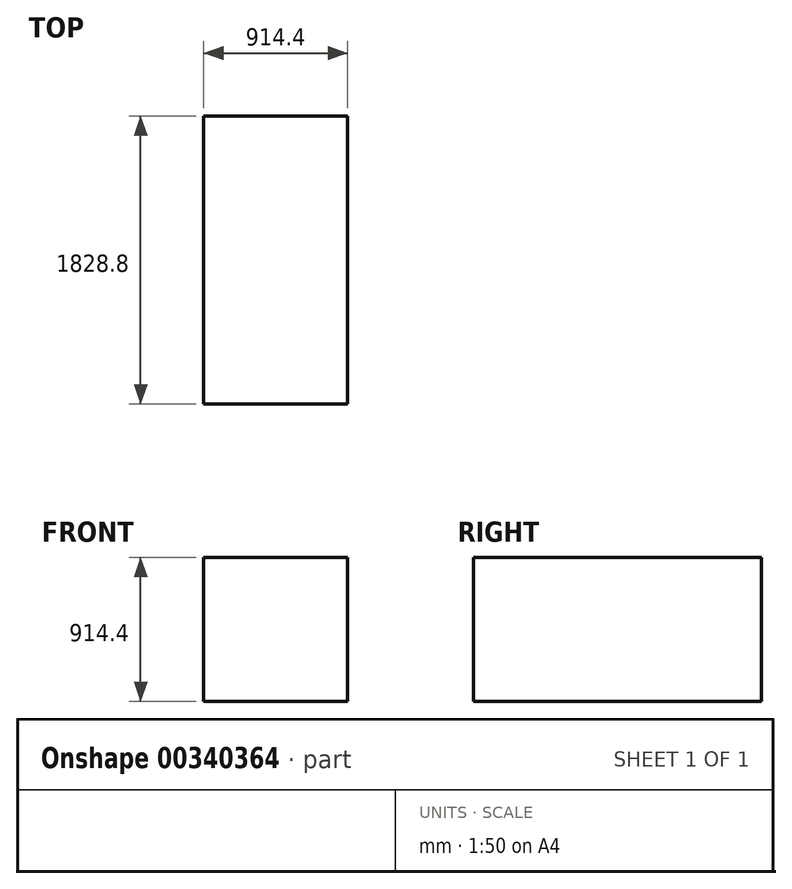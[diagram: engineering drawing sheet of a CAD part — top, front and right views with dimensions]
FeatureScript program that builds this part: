
annotation { "Feature Type Name" : "Feature", "Feature Type Description" : "" }
export const myFeature = defineFeature(function(context is Context, id is Id, definition is map)
    precondition{}
    {
        {
            var Q0;
            Q0=qCreatedBy(makeId("Top.planeOp"),FACE);
            var sketch = newSketch(context, id + "F0", { "sketchPlane" : qUnion([Q0])});
            skLineSegment(sketch, "E0.bottom", {"start": v(457.2, 914.4) * mm, "end": v(-457.2, 914.4) * mm});
            skLineSegment(sketch, "E0.top", {"start": v(457.2, -914.4) * mm, "end": v(-457.2, -914.4) * mm});
            skLineSegment(sketch, "E0.left", {"start": v(457.2, 914.4) * mm, "end": v(457.2, -914.4) * mm});
            skLineSegment(sketch, "E0.right", {"start": v(-457.2, 914.4) * mm, "end": v(-457.2, -914.4) * mm});
            skPoint(sketch, "E0.middle", {"position": v(0, 0) * mm});
            skSolve(sketch);
        }
        {
            var Q0;
            Q0=makeQuery(id+"F0.imprint","IMPRINT",FACE,{"disambiguationData":[TD([[makeQuery(id+"F0.imprint","IMPRINT",EDGE,{"derivedFrom":sQuery(id+"F0.wireOp",EDGE,"E0.bottom")}),1.0]])]});
            extrude(context, id + "F1", {"entities" : qUnion([Q0]), "depth" : 914.4 * mm});
        }
    });
